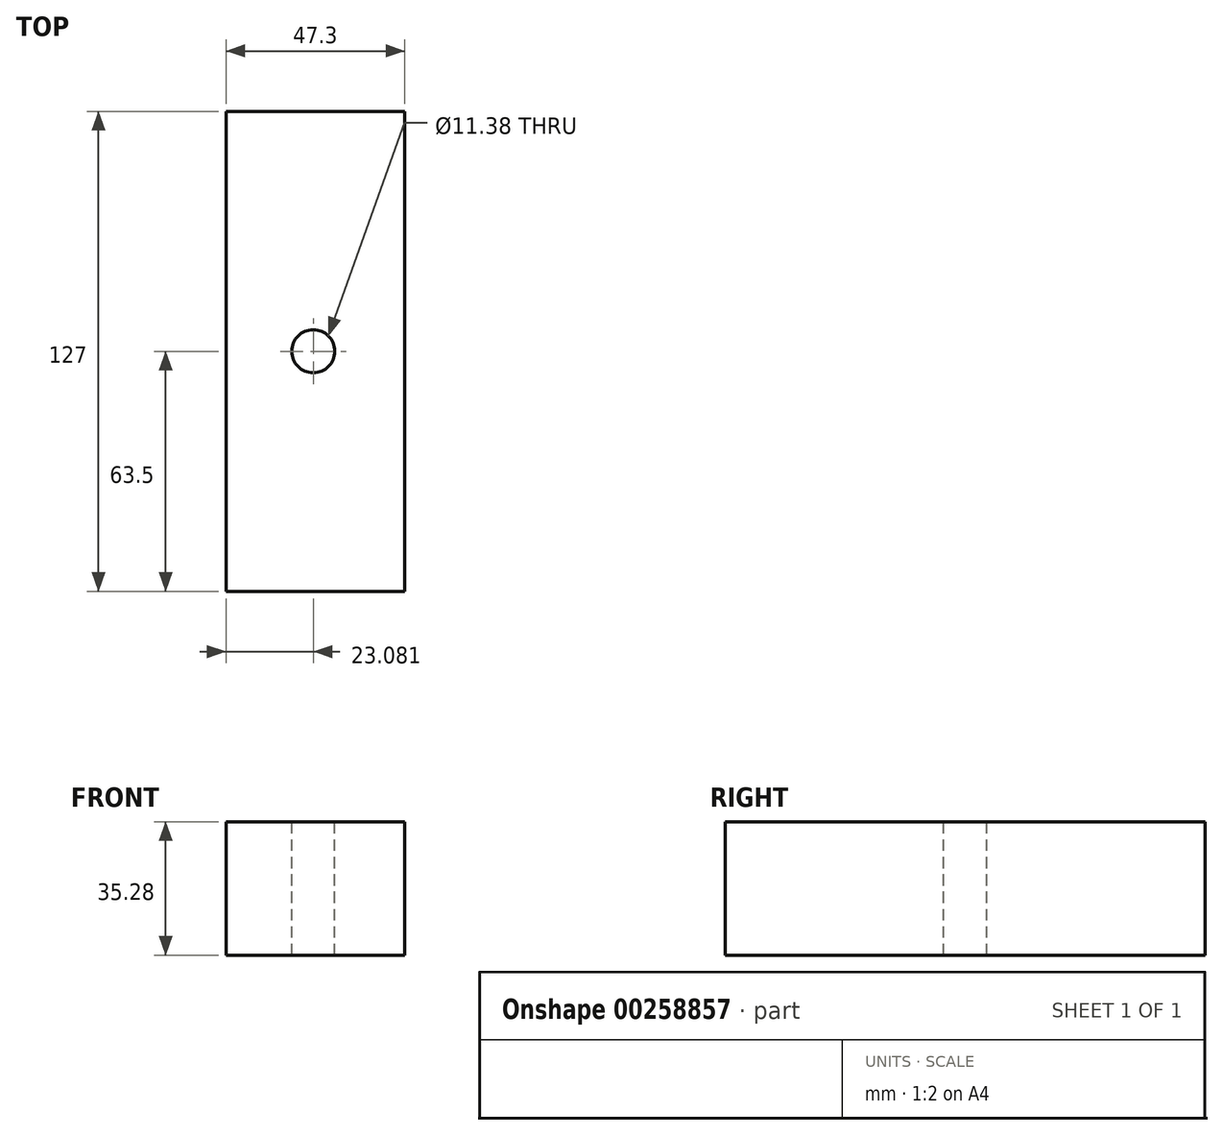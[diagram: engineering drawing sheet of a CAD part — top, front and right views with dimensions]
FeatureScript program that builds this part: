
annotation { "Feature Type Name" : "Feature", "Feature Type Description" : "" }
export const myFeature = defineFeature(function(context is Context, id is Id, definition is map)
    precondition{}
    {
        {
            var Q0;
            Q0=qCreatedBy(makeId("Front.planeOp"),FACE);
            var sketch = newSketch(context, id + "F0", { "sketchPlane" : qUnion([Q0])});
            skLineSegment(sketch, "E0.bottom", {"start": v(-52.65, 7.82) * mm, "end": v(-5.35, 7.82) * mm});
            skLineSegment(sketch, "E0.top", {"start": v(-52.65, -27.46) * mm, "end": v(-5.35, -27.46) * mm});
            skLineSegment(sketch, "E0.left", {"start": v(-52.65, 7.82) * mm, "end": v(-52.65, -27.46) * mm});
            skLineSegment(sketch, "E0.right", {"start": v(-5.35, 7.82) * mm, "end": v(-5.35, -27.46) * mm});
            skSolve(sketch);
        }
        {
            var Q0;
            Q0 = qSketchRegion(id + "F0", true);
            extrude(context, id + "F1", {"entities" : qUnion([Q0]), "depth" : 127 * mm});
        }
        {
            var Q0;
            Q0=makeQuery(id+"F1.opExtrude","SWEPT_FACE",FACE,{"disambiguationData":[OSD([sQuery(id+"F0.wireOp",EDGE,"E0.bottom")])]});
            var sketch = newSketch(context, id + "F2", { "sketchPlane" : qUnion([Q0])});
            skCircle(sketch, "E1", {"center": v(-29.57, -63.5) * mm, "radius": 5.67 * mm});
            skPoint(sketch, "E1.centerSnap0", {"position": v(-52.65, -63.5) * mm});
            skSolve(sketch);
        }
        {
            var Q0;
            Q0=sQuery(id+"F2.wireOp",VERTEX,"E1.center");
            var Q1;
            Q1=makeQuery(id+"F1.opExtrude","SWEPT_BODY",BODY,{"disambiguationData":[OSD([sQuery(id+"F0.wireOp",EDGE,"E0.bottom"),sQuery(id+"F0.wireOp",EDGE,"E0.top"),sQuery(id+"F0.wireOp",EDGE,"E0.left"),sQuery(id+"F0.wireOp",EDGE,"E0.right")])]});
            hole(context, id + "F3", {"style" : HoleStyle.SIMPLE, "endStyle" : HoleEndStyle.THROUGH, "holeDiameter" : 11.38 * mm, "tappedDepth" : 12.7 * mm, "tapClearance" : 3, "locations" : qUnion([Q0]), "scope" : qUnion([Q1])});
        }
    });
